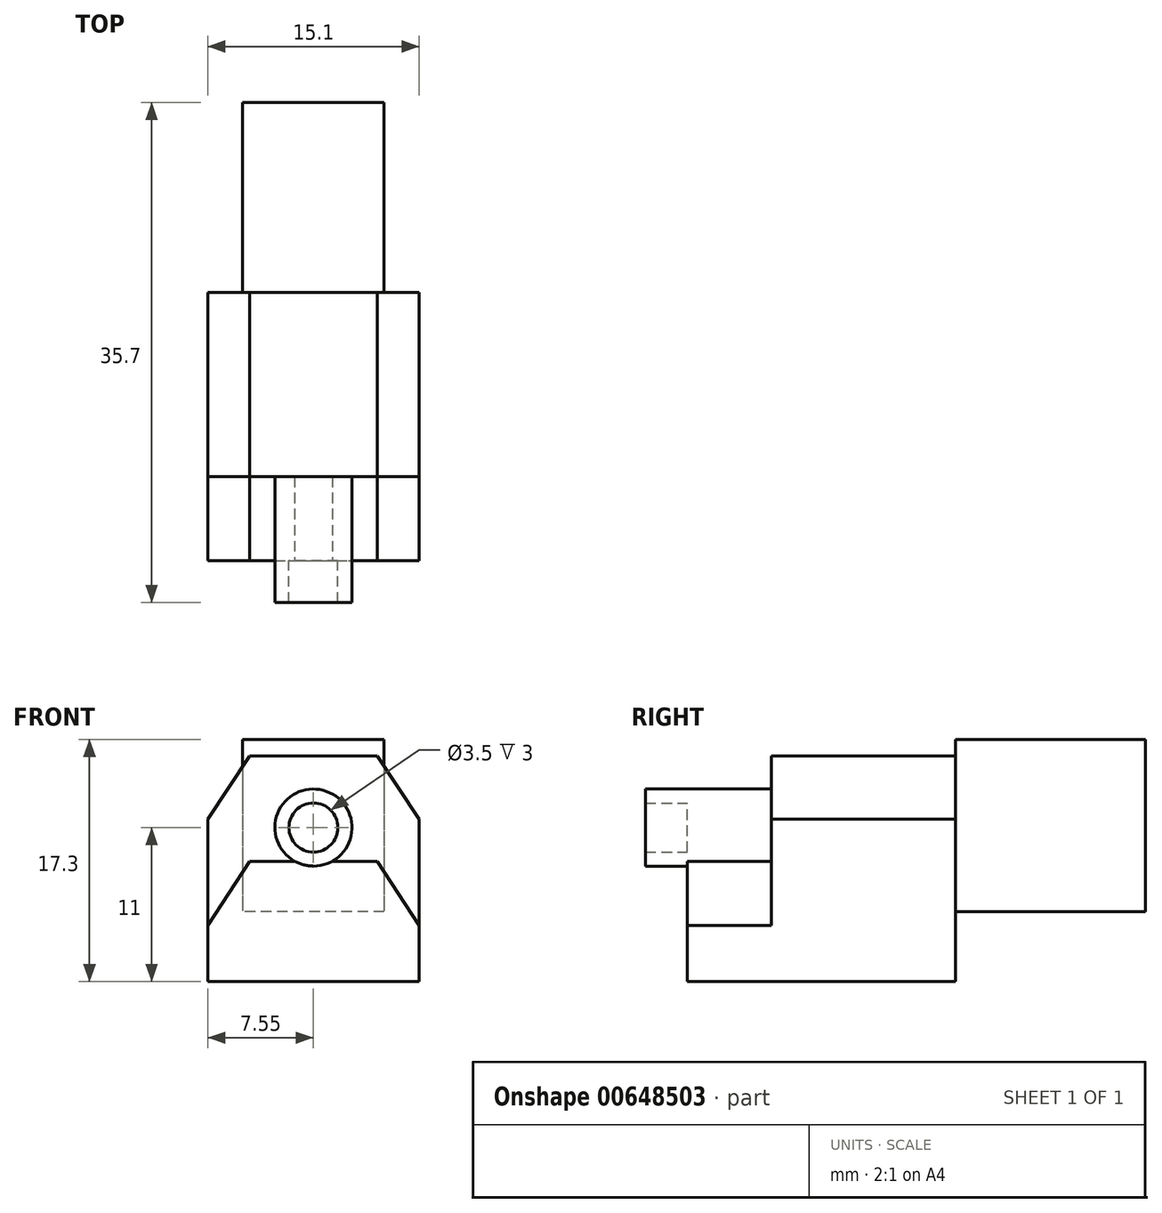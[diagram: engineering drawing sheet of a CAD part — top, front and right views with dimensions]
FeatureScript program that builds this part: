
annotation { "Feature Type Name" : "Feature", "Feature Type Description" : "" }
export const myFeature = defineFeature(function(context is Context, id is Id, definition is map)
    precondition{}
    {
        {
            var Q0;
            Q0=qCreatedBy(makeId("Front.planeOp"),FACE);
            var sketch = newSketch(context, id + "F0", { "sketchPlane" : qUnion([Q0])});
            skLineSegment(sketch, "E0.bottom", {"start": v(-4.55, 8.05) * mm, "end": v(4.55, 8.05) * mm});
            skLineSegment(sketch, "E0.top", {"start": v(-7.55, -8.05) * mm, "end": v(7.55, -8.05) * mm});
            skLineSegment(sketch, "E0.left", {"start": v(-7.55, 3.55) * mm, "end": v(-7.55, -8.05) * mm});
            skLineSegment(sketch, "E0.right", {"start": v(7.55, 3.55) * mm, "end": v(7.55, -8.05) * mm});
            skPoint(sketch, "E0.middle", {"position": v(0, 0) * mm});
            skLineSegment(sketch, "E1", {"start": v(7.55, 3.55) * mm, "end": v(4.55, 8.05) * mm});
            skLineSegment(sketch, "E2", {"start": v(-4.55, 8.05) * mm, "end": v(-7.55, 3.55) * mm});
            skPoint(sketch, "E3.orphan", {"position": v(-7.55, 8.05) * mm});
            skPoint(sketch, "E4.orphan", {"position": v(7.55, 8.05) * mm});
            skSolve(sketch);
        }
        {
            var Q0;
            Q0 = qSketchRegion(id + "F0", true);
            extrude(context, id + "F1", {"entities" : qUnion([Q0]), "depth" : 19.15 * mm, "offsetDistance" : 25 * mm});
        }
        {
            var Q0;
            Q0=makeQuery(id+"F1.opExtrude","CAP_FACE",FACE,{"disambiguationData":[OSD([sQuery(id+"F0.wireOp",EDGE,"E0.bottom"),sQuery(id+"F0.wireOp",EDGE,"E0.top"),sQuery(id+"F0.wireOp",EDGE,"E0.left"),sQuery(id+"F0.wireOp",EDGE,"E0.right"),sQuery(id+"F0.wireOp",EDGE,"E1"),sQuery(id+"F0.wireOp",EDGE,"E2")])],"isStart":false});
            var sketch = newSketch(context, id + "F2", { "sketchPlane" : qUnion([Q0])});
            skCircle(sketch, "E5", {"center": v(0, 2.95) * mm, "radius": 2.75 * mm});
            skCircle(sketch, "E6", {"center": v(0, 2.95) * mm, "radius": 1.75 * mm});
            skSolve(sketch);
        }
        {
            var Q0;
            Q0 = qSketchRegion(id + "F2", true);
            extrude(context, id + "F3", {"entities" : qUnion([Q0]), "operationType" : NewBodyOperationType.ADD, "depth" : 3 * mm, "offsetDistance" : 25 * mm});
        }
        {
            var Q0;
            {var subQ0=sQuery(id+"F0.wireOp",EDGE,"E0.left");var subQ1=sQuery(id+"F0.wireOp",EDGE,"E0.top");var subQ2=sQuery(id+"F0.wireOp",EDGE,"E0.right");var subQ3=sQuery(id+"F0.wireOp",EDGE,"E0.bottom");var subQ4=sQuery(id+"F0.wireOp",EDGE,"E1");var subQ5=sQuery(id+"F0.wireOp",EDGE,"E2");Q0=makeQuery(id+"F3.boolean.opBoolean","SPLIT",FACE,{"disambiguationData":[TD([makeQuery(id+"F1.opExtrude","SWEPT_FACE",FACE,{"disambiguationData":[OSD([subQ3])]})])],"derivedFrom":makeQuery(id+"F1.opExtrude","CAP_FACE",FACE,{"disambiguationData":[OSD([subQ3,subQ1,subQ0,subQ2,subQ4,subQ5])],"isStart":false})});}
            var sketch = newSketch(context, id + "F4", { "sketchPlane" : qUnion([Q0])});
            skLineSegment(sketch, "E7", {"start": v(-4.55, 0.55) * mm, "end": v(-7.55, -4.05) * mm});
            skLineSegment(sketch, "E8.0.0", {"start": v(-7.55, 3.55) * mm, "end": v(-7.55, -4.05) * mm});
            skLineSegment(sketch, "E8.0.2", {"start": v(7.55, -4.05) * mm, "end": v(7.55, 3.55) * mm});
            skLineSegment(sketch, "E8.0.3", {"start": v(7.55, 3.55) * mm, "end": v(4.55, 8.05) * mm});
            skLineSegment(sketch, "E8.0.4", {"start": v(4.55, 8.05) * mm, "end": v(-4.55, 8.05) * mm});
            skLineSegment(sketch, "E8.0.5", {"start": v(-4.55, 8.05) * mm, "end": v(-7.55, 3.55) * mm});
            skLineSegment(sketch, "E9", {"start": v(-4.55, 0.55) * mm, "end": v(-1.34, 0.55) * mm});
            skArc(sketch, "E10.0", {"start": v(1.34, 0.55) * mm, "mid": v(0, 5.7) * mm, "end": v(-1.34, 0.55) * mm});
            skLineSegment(sketch, "E11.trimOffspring", {"start": v(1.34, 0.55) * mm, "end": v(4.55, 0.55) * mm});
            skLineSegment(sketch, "E12.MirrorCS", {"start": v(4.55, 0.55) * mm, "end": v(7.55, -4.05) * mm});
            skPoint(sketch, "E8.0.1.start.orphan", {"position": v(-7.55, -8.05) * mm});
            skPoint(sketch, "E13.orphan", {"position": v(7.55, -8.05) * mm});
            skSolve(sketch);
        }
        {
            var Q0;
            Q0 = qSketchRegion(id + "F4", true);
            extrude(context, id + "F5", {"entities" : qUnion([Q0]), "operationType" : NewBodyOperationType.REMOVE, "oppositeDirection" : true, "depth" : 6 * mm, "offsetDistance" : 25 * mm});
        }
        {
            var Q0;
            Q0=makeQuery(id+"F1.opExtrude","CAP_FACE",FACE,{"disambiguationData":[OSD([sQuery(id+"F0.wireOp",EDGE,"E0.bottom"),sQuery(id+"F0.wireOp",EDGE,"E0.top"),sQuery(id+"F0.wireOp",EDGE,"E0.left"),sQuery(id+"F0.wireOp",EDGE,"E0.right"),sQuery(id+"F0.wireOp",EDGE,"E1"),sQuery(id+"F0.wireOp",EDGE,"E2")])],"isStart":true});
            var sketch = newSketch(context, id + "F6", { "sketchPlane" : qUnion([Q0])});
            skLineSegment(sketch, "E14.bottom", {"start": v(-5.05, 9.25) * mm, "end": v(5.05, 9.25) * mm});
            skLineSegment(sketch, "E14.top", {"start": v(-5.05, -3.05) * mm, "end": v(5.05, -3.05) * mm});
            skLineSegment(sketch, "E14.left", {"start": v(-5.05, 9.25) * mm, "end": v(-5.05, -3.05) * mm});
            skLineSegment(sketch, "E14.right", {"start": v(5.05, 9.25) * mm, "end": v(5.05, -3.05) * mm});
            skSolve(sketch);
        }
        {
            var Q0;
            Q0 = qSketchRegion(id + "F6", true);
            extrude(context, id + "F7", {"entities" : qUnion([Q0]), "operationType" : NewBodyOperationType.ADD, "depth" : 13.55 * mm, "offsetDistance" : 25 * mm});
        }
    });
